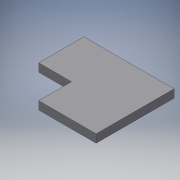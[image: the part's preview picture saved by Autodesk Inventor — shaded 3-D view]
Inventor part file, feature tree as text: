
AUTODESK INVENTOR PART (.ipt)
format: ipt  version: 2018 (Build 220112000, 112)  size: 107,008 bytes
history: native  units: mm
features: extrude x1, fillet x1, sketch x1
ambient origin geometry x8: Origin, YZ Plane, XZ Plane, XY Plane, X Axis, Y Axis, Z Axis, Center Point
bodies: Solido1 (feature_tree)
feature tree (3):
  extrude  "Estrusione1"  Depth=40.0mm
  fillet  "Raccordo1"  Radius=40.0mm
  sketch  "Schizzo1"
